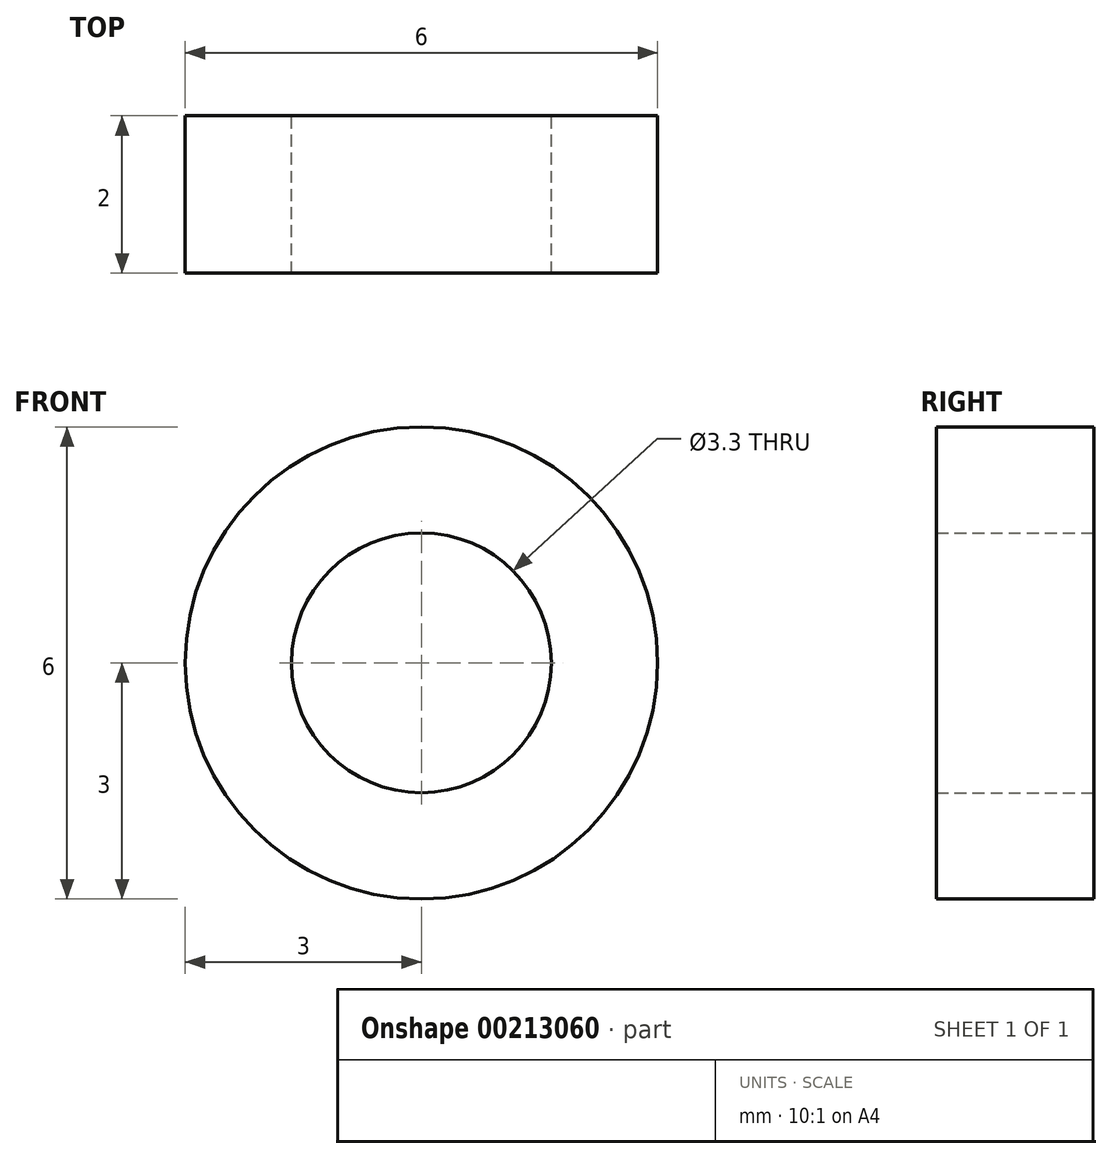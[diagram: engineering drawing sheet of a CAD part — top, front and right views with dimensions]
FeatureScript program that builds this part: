
annotation { "Feature Type Name" : "Feature", "Feature Type Description" : "" }
export const myFeature = defineFeature(function(context is Context, id is Id, definition is map)
    precondition{}
    {
        {
            var Q0;
            Q0=qCreatedBy(makeId("Front.planeOp"),FACE);
            var sketch = newSketch(context, id + "F0", { "sketchPlane" : qUnion([Q0])});
            skCircle(sketch, "E0", {"center": v(0, 0) * mm, "radius": 1.65 * mm});
            skCircle(sketch, "E1", {"center": v(0, 0) * mm, "radius": 3 * mm});
            skSolve(sketch);
        }
        {
            var Q0;
            Q0=makeQuery(id+"F0.imprint","IMPRINT",FACE,{"disambiguationData":[TD([[makeQuery(id+"F0.imprint","IMPRINT",EDGE,{"derivedFrom":sQuery(id+"F0.wireOp",EDGE,"E0")}),-1.0]])]});
            extrude(context, id + "F1", {"entities" : qUnion([Q0]), "depth" : 2 * mm});
        }
    });
